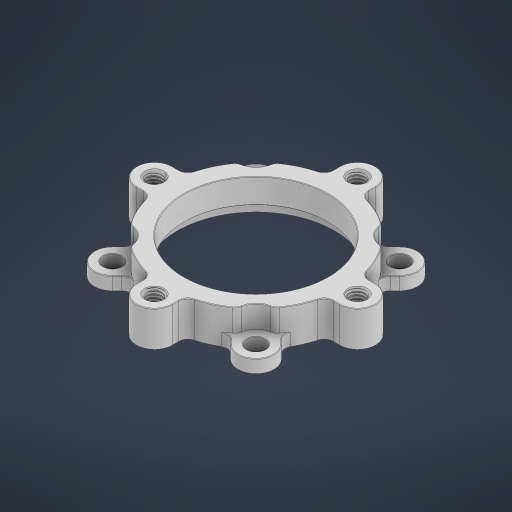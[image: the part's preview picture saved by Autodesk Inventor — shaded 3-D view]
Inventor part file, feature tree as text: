
AUTODESK INVENTOR PART (.ipt)
format: ipt  version: 2023 (Build 270158000, 158)  size: 1,471,488 bytes
history: native  units: in
note: dims shown in document units (in); Inventor stores cm internally (conversion verified against a paired STEP export)
features: chamfer x1
ambient origin geometry x8: Origin, YZ Plane, XZ Plane, XY Plane, X Axis, Y Axis, Z Axis, Center Point
bodies: Solid1 (feature_tree)
feature tree (1):
  chamfer  "Chamfer4"  [1 undecoded]
note: 1 required parameter value undecoded (feature->parameter linkage not recoverable at this tier; creation-order binding heuristic only, values carry confidence <= 0.55)
